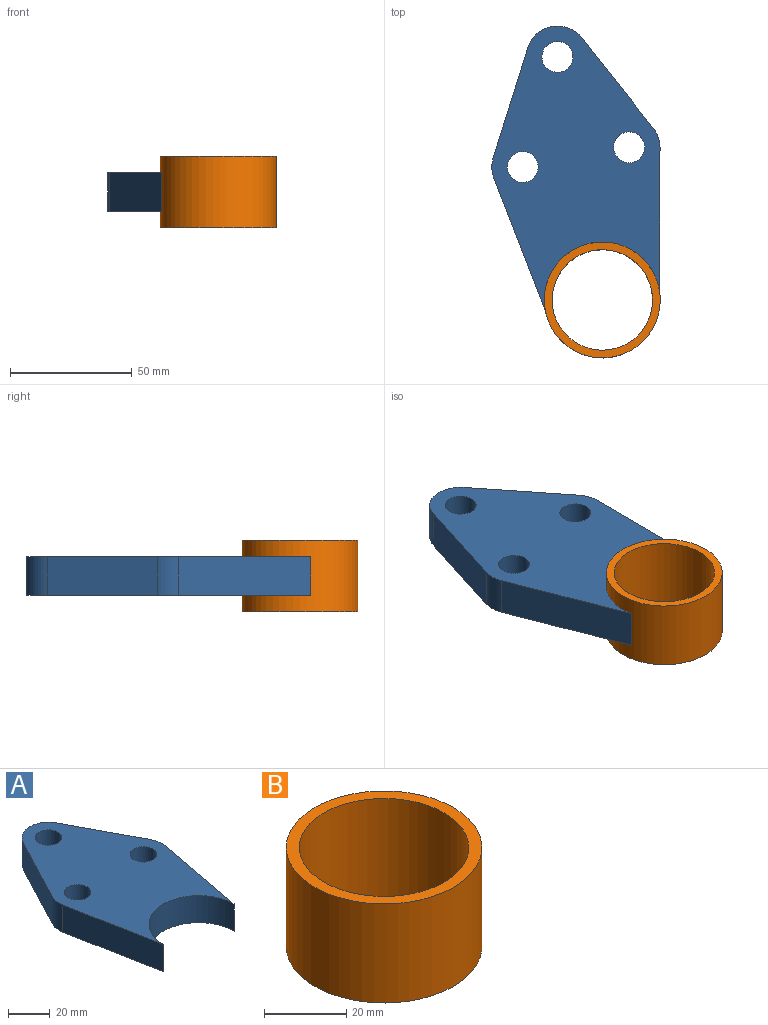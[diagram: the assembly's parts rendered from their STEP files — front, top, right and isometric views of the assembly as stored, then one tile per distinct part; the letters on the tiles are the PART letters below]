
ASSEMBLY  parts=2 mates=1
PART A: 13 faces, bbox 69.9x114.3x15.9 mm
  f0: cylinder r=23.81mm len=47.63mm, axis (0,0,-1), area 1187.6mm2, adj f1,f9,f11,f12
  f1: plane 57.32x15.88mm, normal (0.98,-0.19,0), area 926.2mm2, adj f0,f2,f11,f12
  f2: cylinder r=12.7mm len=15.88mm, axis (0,0,-1), area 136.2mm2, adj f1,f3,f11,f12
  f3: plane 41.91x22.23mm, normal (0.88,0.47,0), area 753.1mm2, adj f2,f4,f11,f12
  f4: cylinder r=12.7mm len=22.44mm, axis (0,0,-1), area 436.8mm2, adj f3,f5,f11,f12
  f5: plane 41.91x22.23mm, normal (-0.88,0.47,0), area 753.1mm2, adj f4,f6,f11,f12
  f6: cylinder r=12.7mm len=15.88mm, axis (0,0,-1), area 136.2mm2, adj f5,f9,f11,f12
  f7: cylinder r=6.35mm len=15.88mm, axis (0,0,-1), area 633.4mm2, adj f11,f12
  f8: cylinder r=6.35mm len=15.88mm, axis (0,0,-1), area 633.4mm2, adj f11,f12
  f9: plane 57.32x15.88mm, normal (-0.98,-0.19,0), area 926.2mm2, adj f0,f6,f11,f12
  f10: cylinder r=6.35mm len=15.88mm, axis (0,0,-1), area 633.4mm2, adj f11,f12
  f11: plane 114.3x69.85mm, normal (0,0,1), area 4638.2mm2, adj f0,f1,f2,f3,f4,f5,f6,f7
  f12: plane 114.3x69.85mm, normal (0,0,-1), area 4638.2mm2, adj f0,f1,f2,f3,f4,f5,f6,f7
PART B: 4 faces, bbox 47.6x47.6x29.5 mm
  f0: cylinder r=20.64mm len=41.28mm, axis (0,0,-1), area 3823.9mm2, adj f2,f3
  f1: cylinder r=23.81mm len=47.63mm, axis (0,0,-1), area 4412.2mm2, adj f2,f3
  f2: plane 47.63x47.63mm, normal (0,0,1), area 443.4mm2, adj f0,f1
  f3: plane 47.63x47.63mm, normal (0,0,-1), area 443.4mm2, adj f0,f1
PLACE A rot(axis=(0,0,1),10.5deg) t=(-26.21,249.05,-186.32)mm
PLACE B rot(axis=(0,0,1),10.5deg) t=(-26.21,249.05,-186.32)mm
MATE fastened A.f0 <-> B.f0  axis (0,0,-1) through (-15.38,190.35,-186.32)mm
